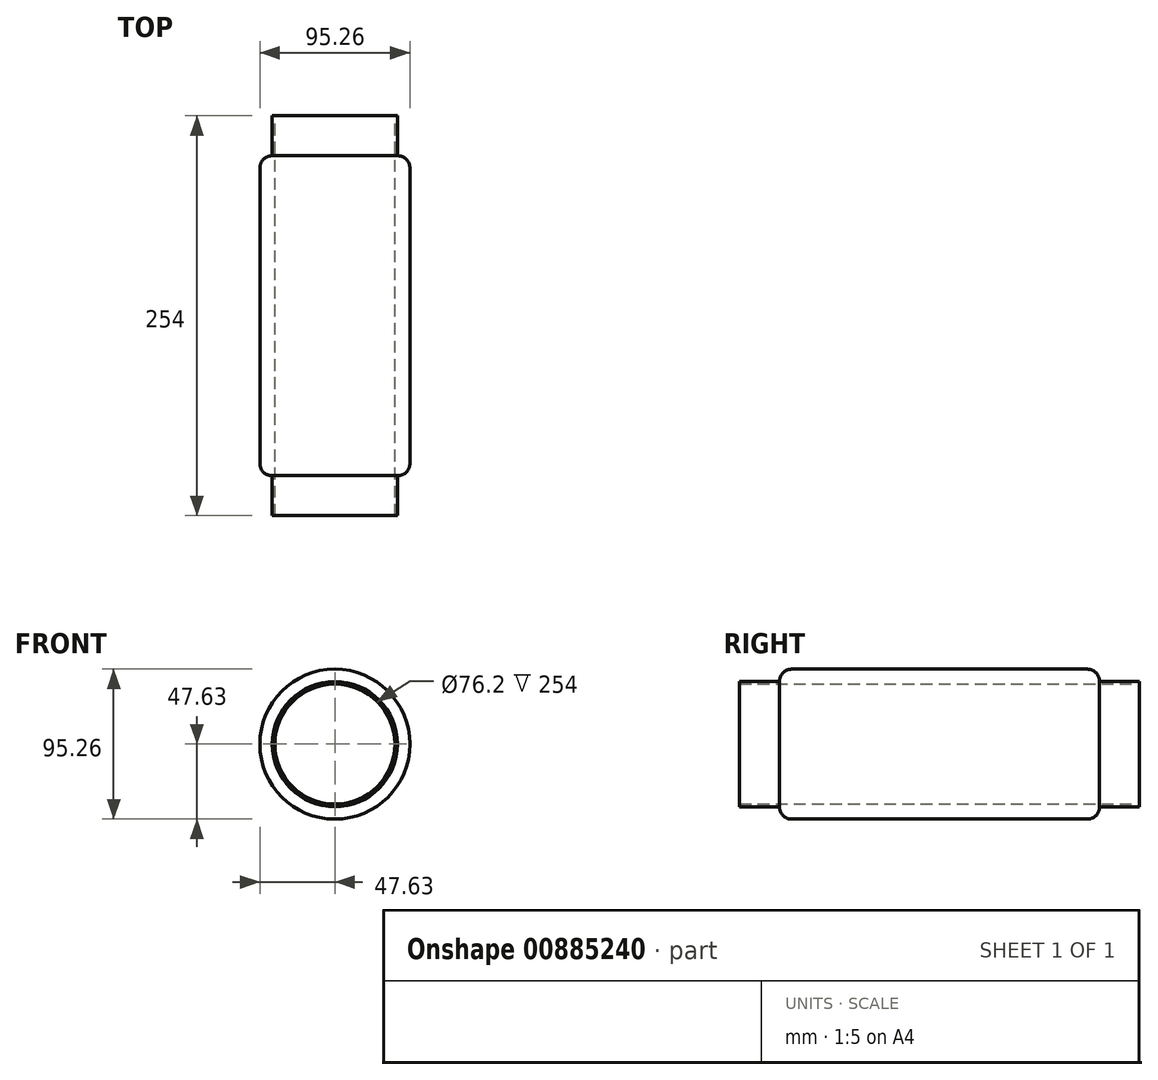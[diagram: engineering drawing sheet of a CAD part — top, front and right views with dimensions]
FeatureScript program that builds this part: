
annotation { "Feature Type Name" : "Feature", "Feature Type Description" : "" }
export const myFeature = defineFeature(function(context is Context, id is Id, definition is map)
    precondition{}
    {
        {
            var Q0;
            Q0=qCreatedBy(makeId("Front.planeOp"),FACE);
            var sketch = newSketch(context, id + "F0", { "sketchPlane" : qUnion([Q0])});
            skCircle(sketch, "E0", {"center": v(0, 0) * mm, "radius": 39.75 * mm});
            skCircle(sketch, "E1", {"center": v(0, 0) * mm, "radius": 38.1 * mm});
            skSolve(sketch);
        }
        {
            var Q0;
            Q0=makeQuery(id+"F0.imprint","IMPRINT",FACE,{"disambiguationData":[TD([[makeQuery(id+"F0.imprint","IMPRINT",EDGE,{"derivedFrom":sQuery(id+"F0.wireOp",EDGE,"E0")}),1.0]])]});
            extrude(context, id + "F1", {"entities" : qUnion([Q0]), "endBound" : BoundingType.SYMMETRIC, "depth" : 254 * mm, "offsetDistance" : 25.4 * mm});
        }
        {
            var Q0;
            Q0=qCreatedBy(makeId("Front.planeOp"),FACE);
            var sketch = newSketch(context, id + "F2", { "sketchPlane" : qUnion([Q0])});
            skCircle(sketch, "E2", {"center": v(0, 0) * mm, "radius": 39.75 * mm});
            skCircle(sketch, "E3", {"center": v(0, 0) * mm, "radius": 47.63 * mm});
            skSolve(sketch);
        }
        {
            var Q0;
            Q0=makeQuery(id+"F2.imprint","IMPRINT",FACE,{"disambiguationData":[TD([[makeQuery(id+"F2.imprint","IMPRINT",EDGE,{"derivedFrom":sQuery(id+"F2.wireOp",EDGE,"E2")}),-1.0]])]});
            extrude(context, id + "F3", {"entities" : qUnion([Q0]), "operationType" : NewBodyOperationType.ADD, "endBound" : BoundingType.SYMMETRIC, "depth" : 203.2 * mm, "offsetDistance" : 25.4 * mm});
        }
        {
            var Q0;
            Q0=makeQuery(id+"F3.opExtrude","CAP_EDGE",EDGE,{"disambiguationData":[OSD([sQuery(id+"F2.wireOp",EDGE,"E3")])],"isStart":false});
            var Q1;
            Q1=makeQuery(id+"F3.opExtrude","CAP_EDGE",EDGE,{"disambiguationData":[OSD([sQuery(id+"F2.wireOp",EDGE,"E3")])],"isStart":true});
            fillet(context, id + "F4", {"entities" : qUnion([Q0, Q1]), "radius" : 7.62 * mm, "tangentPropagation" : true, "allowEdgeOverflow" : false});
        }
    });
